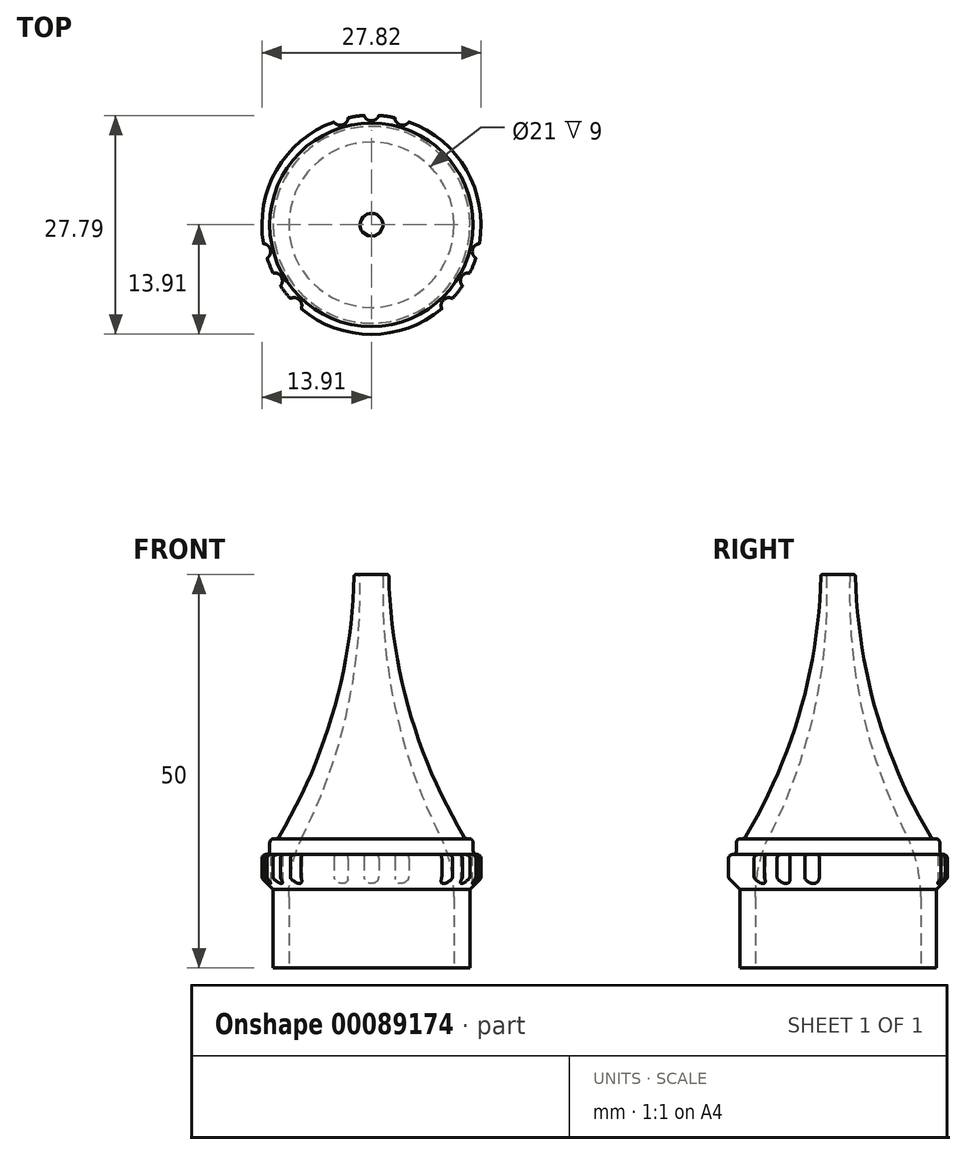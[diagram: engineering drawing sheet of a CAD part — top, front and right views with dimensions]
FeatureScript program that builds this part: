
annotation { "Feature Type Name" : "Feature", "Feature Type Description" : "" }
export const myFeature = defineFeature(function(context is Context, id is Id, definition is map)
    precondition{}
    {
        {
            var Q0;
            Q0=qCreatedBy(makeId("Front.planeOp"),FACE);
            var sketch = newSketch(context, id + "F0", { "sketchPlane" : qUnion([Q0])});
            skArc(sketch, "E0", {"start": v(-11.91, 16.41) * mm, "mid": v(-4.84, 32.57) * mm, "end": v(-2.2, 50) * mm});
            skLineSegment(sketch, "E1", {"start": v(-11.91, 16.41) * mm, "end": v(-12.91, 16.41) * mm});
            skLineSegment(sketch, "E2", {"start": v(-12.91, 16.41) * mm, "end": v(-12.91, 14.41) * mm});
            skLineSegment(sketch, "E3", {"start": v(-12.91, 14.41) * mm, "end": v(-13.91, 14.41) * mm});
            skLineSegment(sketch, "E4", {"start": v(-13.91, 14.41) * mm, "end": v(-13.91, 11.41) * mm});
            skLineSegment(sketch, "E5", {"start": v(-13.91, 11.41) * mm, "end": v(-12.5, 10) * mm});
            skLineSegment(sketch, "E6", {"start": v(-12.5, 10) * mm, "end": v(-12.5, 0) * mm});
            skLineSegment(sketch, "E7", {"start": v(-12.5, 0) * mm, "end": v(-10.5, 0) * mm});
            skLineSegment(sketch, "E8", {"start": v(-10.5, 0) * mm, "end": v(-10.5, 9) * mm});
            skArc(sketch, "E9", {"start": v(-8.91, 16.41) * mm, "mid": v(-3.06, 32.73) * mm, "end": v(-1.5, 50) * mm});
            skLineSegment(sketch, "E10", {"start": v(-2.2, 50) * mm, "end": v(-1.5, 50) * mm});
            skArc(sketch, "E11", {"start": v(-9.1, 16.03) * mm, "mid": v(-10.14, 12.58) * mm, "end": v(-10.5, 9) * mm});
            skArc(sketch, "E12", {"start": v(-8.91, 16.41) * mm, "mid": v(-9, 16.22) * mm, "end": v(-9.1, 16.03) * mm});
            skSolve(sketch);
        }
        {
            var Q0;
            Q0=qCreatedBy(makeId("Top.planeOp"),FACE);
            var sketch = newSketch(context, id + "F1", { "sketchPlane" : qUnion([Q0])});
            skCircle(sketch, "E13", {"center": v(0, 0) * mm, "radius": 22.52 * mm, "construction": true});
            skSolve(sketch);
        }
        {
            var Q0;
            Q0=qSketchRegion(id+"F0",true);
            var Q1;
            Q1=sQuery(id+"F1.wireOp",EDGE,"E13");
            revolve(context, id + "F2", {"entities" : qUnion([Q0]), "axis" : qUnion([Q1]), "revolveType" : RevolveType.FULL});
        }
        {
            var Q0;
            Q0=makeQuery(id+"F2.opRevolve","SWEPT_EDGE",EDGE,{"disambiguationData":[OSD([sQuery(id+"F0.wireOp",EDGE,"E3"),sQuery(id+"F0.wireOp",EDGE,"E4")])]});
            var Q1;
            Q1=makeQuery(id+"F2.opRevolve","SWEPT_EDGE",EDGE,{"disambiguationData":[OSD([sQuery(id+"F0.wireOp",EDGE,"E4"),sQuery(id+"F0.wireOp",EDGE,"E5")])]});
            var Q2;
            Q2=makeQuery(id+"F2.opRevolve","SWEPT_EDGE",EDGE,{"disambiguationData":[OSD([sQuery(id+"F0.wireOp",EDGE,"E1"),sQuery(id+"F0.wireOp",EDGE,"E2")])]});
            var Q3;
            Q3=makeQuery(id+"F2.opRevolve","SWEPT_EDGE",EDGE,{"disambiguationData":[OSD([sQuery(id+"F0.wireOp",EDGE,"E0"),sQuery(id+"F0.wireOp",EDGE,"E1")])]});
            var Q4;
            Q4=makeQuery(id+"F2.opRevolve","SWEPT_EDGE",EDGE,{"disambiguationData":[OSD([sQuery(id+"F0.wireOp",EDGE,"E2"),sQuery(id+"F0.wireOp",EDGE,"E3")])]});
            fillet(context, id + "F3", {"entities" : qUnion([Q0, Q1, Q2, Q3, Q4]), "radius" : 0.5 * mm, "tangentPropagation" : true, "allowEdgeOverflow" : false});
        }
        {
            var Q0;
            Q0=makeQuery(id+"F2.opRevolve","SWEPT_EDGE",EDGE,{"disambiguationData":[OSD([sQuery(id+"F0.wireOp",EDGE,"E0"),sQuery(id+"F0.wireOp",EDGE,"E10")])]});
            var Q1;
            Q1=makeQuery(id+"F2.opRevolve","SWEPT_EDGE",EDGE,{"disambiguationData":[OSD([sQuery(id+"F0.wireOp",EDGE,"E9"),sQuery(id+"F0.wireOp",EDGE,"E10")])]});
            fillet(context, id + "F4", {"entities" : qUnion([Q0, Q1]), "radius" : 0.25 * mm, "tangentPropagation" : true, "allowEdgeOverflow" : false});
        }
        {
            var Q0;
            Q0=qCreatedBy(makeId("Top.planeOp"),FACE);
            var sketch = newSketch(context, id + "F5", { "sketchPlane" : qUnion([Q0])});
            skCircle(sketch, "E14", {"center": v(0, 14.21) * mm, "radius": 1 * mm});
            skCircle(sketch, "E15", {"center": v(-3.96, 13.65) * mm, "radius": 1 * mm});
            skCircle(sketch, "E16", {"center": v(3.96, 13.65) * mm, "radius": 1 * mm});
            skCircle(sketch, "E17", {"center": v(0, 0) * mm, "radius": 14.21 * mm, "construction": true});
            skCircle(sketch, "E18.1.0", {"center": v(-9.84, -10.26) * mm, "radius": 1 * mm});
            skCircle(sketch, "E18.1.1", {"center": v(-12.3, -7.1) * mm, "radius": 1 * mm});
            skCircle(sketch, "E18.1.2", {"center": v(-13.8, -3.4) * mm, "radius": 1 * mm});
            skCircle(sketch, "E18.2.0", {"center": v(13.8, -3.4) * mm, "radius": 1 * mm});
            skCircle(sketch, "E18.2.1", {"center": v(12.3, -7.1) * mm, "radius": 1 * mm});
            skCircle(sketch, "E18.2.2", {"center": v(9.84, -10.26) * mm, "radius": 1 * mm});
            skSolve(sketch);
        }
        {
            var Q0;
            Q0=qSketchRegion(id+"F5",true);
            extrude(context, id + "F6", {"entities" : qUnion([Q0]), "operationType" : NewBodyOperationType.REMOVE, "depth" : 25 * mm});
        }
    });
